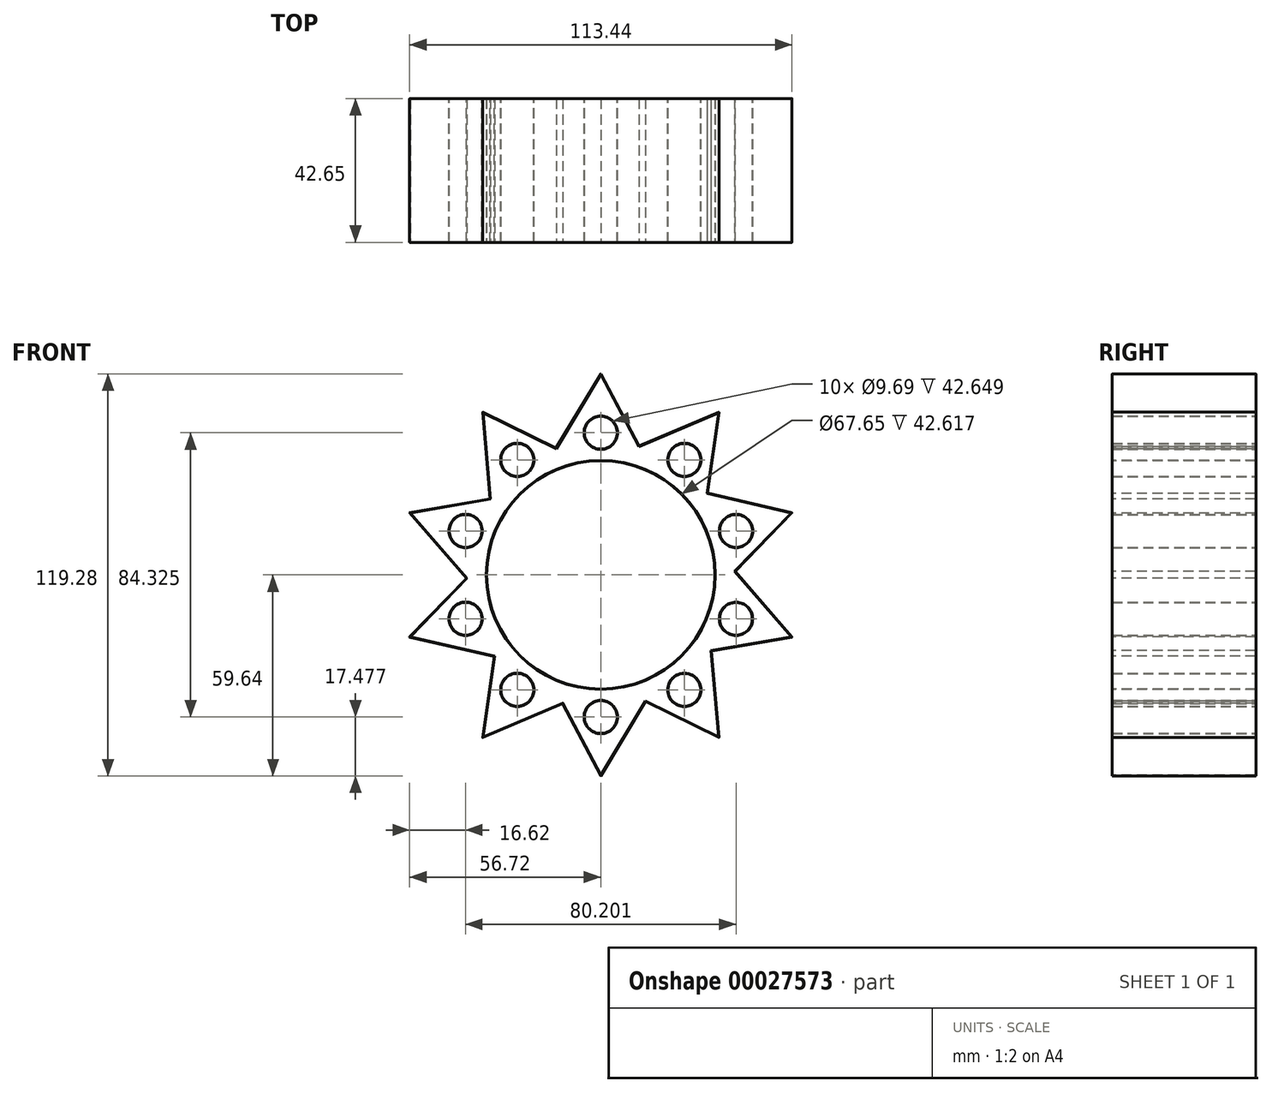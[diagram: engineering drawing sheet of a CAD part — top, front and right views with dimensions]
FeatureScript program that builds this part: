
annotation { "Feature Type Name" : "Feature", "Feature Type Description" : "" }
export const myFeature = defineFeature(function(context is Context, id is Id, definition is map)
    precondition{}
    {
        {
            var Q0;
            Q0=qCreatedBy(makeId("Front.planeOp"),FACE);
            var sketch = newSketch(context, id + "F0", { "sketchPlane" : qUnion([Q0])});
            skCircle(sketch, "E0", {"center": v(0, 0) * mm, "radius": 33.83 * mm});
            skLineSegment(sketch, "E1", {"start": v(-15.28, 34.27) * mm, "end": v(13.84, 33.45) * mm});
            skLineSegment(sketch, "E2", {"start": v(13.84, 33.45) * mm, "end": v(0, 59.67) * mm});
            skLineSegment(sketch, "E3", {"start": v(0, 59.67) * mm, "end": v(-15.28, 34.27) * mm});
            skLineSegment(sketch, "E4.1.0", {"start": v(-8.46, 35.2) * mm, "end": v(-35.07, 48.28) * mm});
            skLineSegment(sketch, "E4.1.1", {"start": v(-35.07, 48.28) * mm, "end": v(-32.5, 18.74) * mm});
            skLineSegment(sketch, "E4.2.0", {"start": v(-27.53, 23.5) * mm, "end": v(-56.75, 18.44) * mm});
            skLineSegment(sketch, "E4.2.1", {"start": v(-56.75, 18.44) * mm, "end": v(-37.31, -3.94) * mm});
            skLineSegment(sketch, "E4.3.0", {"start": v(-36.09, 2.83) * mm, "end": v(-56.75, -18.44) * mm});
            skLineSegment(sketch, "E4.3.1", {"start": v(-56.75, -18.44) * mm, "end": v(-27.87, -25.12) * mm});
            skLineSegment(sketch, "E4.4.0", {"start": v(-30.86, -18.92) * mm, "end": v(-35.07, -48.28) * mm});
            skLineSegment(sketch, "E4.4.1", {"start": v(-35.07, -48.28) * mm, "end": v(-7.78, -36.7) * mm});
            skLineSegment(sketch, "E4.5.0", {"start": v(-13.84, -33.45) * mm, "end": v(0, -59.67) * mm});
            skLineSegment(sketch, "E4.5.1", {"start": v(0, -59.67) * mm, "end": v(15.28, -34.27) * mm});
            skLineSegment(sketch, "E4.6.0", {"start": v(8.46, -35.2) * mm, "end": v(35.07, -48.28) * mm});
            skLineSegment(sketch, "E4.6.1", {"start": v(35.07, -48.28) * mm, "end": v(32.5, -18.74) * mm});
            skLineSegment(sketch, "E4.7.0", {"start": v(27.53, -23.5) * mm, "end": v(56.75, -18.44) * mm});
            skLineSegment(sketch, "E4.7.1", {"start": v(56.75, -18.44) * mm, "end": v(37.31, 3.94) * mm});
            skLineSegment(sketch, "E4.8.0", {"start": v(36.09, -2.83) * mm, "end": v(56.75, 18.44) * mm});
            skLineSegment(sketch, "E4.8.1", {"start": v(56.75, 18.44) * mm, "end": v(27.87, 25.12) * mm});
            skLineSegment(sketch, "E4.9.0", {"start": v(30.86, 18.92) * mm, "end": v(35.07, 48.28) * mm});
            skLineSegment(sketch, "E4.9.1", {"start": v(35.07, 48.28) * mm, "end": v(7.78, 36.7) * mm});
            skSolve(sketch);
        }
        {
            var Q0;
            Q0 = qSketchRegion(id + "F0", true);
            extrude(context, id + "F1", {"entities" : qUnion([Q0]), "oppositeDirection" : true, "depth" : 42.65 * mm});
        }
        {
            var Q0;
            Q0=makeQuery(id+"F1.opExtrude","CAP_FACE",FACE,{"disambiguationData":[OSD([sQuery(id+"F0.wireOp",EDGE,"E0"),sQuery(id+"F0.wireOp",EDGE,"E2"),sQuery(id+"F0.wireOp",EDGE,"E3"),sQuery(id+"F0.wireOp",EDGE,"E4.1.0"),sQuery(id+"F0.wireOp",EDGE,"E4.1.1"),sQuery(id+"F0.wireOp",EDGE,"E4.2.0"),sQuery(id+"F0.wireOp",EDGE,"E4.2.1"),sQuery(id+"F0.wireOp",EDGE,"E4.3.0"),sQuery(id+"F0.wireOp",EDGE,"E4.3.1"),sQuery(id+"F0.wireOp",EDGE,"E4.4.0"),sQuery(id+"F0.wireOp",EDGE,"E4.4.1"),sQuery(id+"F0.wireOp",EDGE,"E4.5.0"),sQuery(id+"F0.wireOp",EDGE,"E4.5.1"),sQuery(id+"F0.wireOp",EDGE,"E4.6.0"),sQuery(id+"F0.wireOp",EDGE,"E4.6.1"),sQuery(id+"F0.wireOp",EDGE,"E4.7.0"),sQuery(id+"F0.wireOp",EDGE,"E4.7.1"),sQuery(id+"F0.wireOp",EDGE,"E4.8.0"),sQuery(id+"F0.wireOp",EDGE,"E4.8.1"),sQuery(id+"F0.wireOp",EDGE,"E4.9.0"),sQuery(id+"F0.wireOp",EDGE,"E4.9.1")])],"isStart":false});
            var sketch = newSketch(context, id + "F2", { "sketchPlane" : qUnion([Q0])});
            skCircle(sketch, "E5", {"center": v(-24.78, -34.11) * mm, "radius": 4.85 * mm});
            skCircle(sketch, "E6.1.0", {"center": v(0, -42.16) * mm, "radius": 4.85 * mm});
            skCircle(sketch, "E6.2.0", {"center": v(24.79, -34.1) * mm, "radius": 4.85 * mm});
            skCircle(sketch, "E6.3.0", {"center": v(40.1, -13.02) * mm, "radius": 4.85 * mm});
            skCircle(sketch, "E6.4.0", {"center": v(40.1, 13.03) * mm, "radius": 4.85 * mm});
            skCircle(sketch, "E6.5.0", {"center": v(24.78, 34.11) * mm, "radius": 4.85 * mm});
            skCircle(sketch, "E6.6.0", {"center": v(0, 42.16) * mm, "radius": 4.85 * mm});
            skCircle(sketch, "E6.7.0", {"center": v(-24.79, 34.1) * mm, "radius": 4.85 * mm});
            skCircle(sketch, "E6.8.0", {"center": v(-40.1, 13.02) * mm, "radius": 4.85 * mm});
            skCircle(sketch, "E6.9.0", {"center": v(-40.1, -13.03) * mm, "radius": 4.85 * mm});
            skPoint(sketch, "E6.center", {"position": v(0, 0) * mm});
            skSolve(sketch);
        }
        {
            var Q0;
            Q0 = qSketchRegion(id + "F2", true);
            extrude(context, id + "F3", {"entities" : qUnion([Q0]), "operationType" : NewBodyOperationType.REMOVE, "endBound" : BoundingType.THROUGH_ALL, "oppositeDirection" : true, "depth" : 25.4 * mm});
        }
        {
            var Q0;
            Q0=makeQuery(id+"F1.opExtrude","CAP_FACE",FACE,{"disambiguationData":[OSD([sQuery(id+"F0.wireOp",EDGE,"E0"),sQuery(id+"F0.wireOp",EDGE,"E2"),sQuery(id+"F0.wireOp",EDGE,"E3"),sQuery(id+"F0.wireOp",EDGE,"E4.1.0"),sQuery(id+"F0.wireOp",EDGE,"E4.1.1"),sQuery(id+"F0.wireOp",EDGE,"E4.2.0"),sQuery(id+"F0.wireOp",EDGE,"E4.2.1"),sQuery(id+"F0.wireOp",EDGE,"E4.3.0"),sQuery(id+"F0.wireOp",EDGE,"E4.3.1"),sQuery(id+"F0.wireOp",EDGE,"E4.4.0"),sQuery(id+"F0.wireOp",EDGE,"E4.4.1"),sQuery(id+"F0.wireOp",EDGE,"E4.5.0"),sQuery(id+"F0.wireOp",EDGE,"E4.5.1"),sQuery(id+"F0.wireOp",EDGE,"E4.6.0"),sQuery(id+"F0.wireOp",EDGE,"E4.6.1"),sQuery(id+"F0.wireOp",EDGE,"E4.7.0"),sQuery(id+"F0.wireOp",EDGE,"E4.7.1"),sQuery(id+"F0.wireOp",EDGE,"E4.8.0"),sQuery(id+"F0.wireOp",EDGE,"E4.8.1"),sQuery(id+"F0.wireOp",EDGE,"E4.9.0"),sQuery(id+"F0.wireOp",EDGE,"E4.9.1")])],"isStart":true});
            shell(context, id + "F4", {"entities" : qUnion([Q0]), "thickness" : 0.13 * mm});
        }
        {
            var Q0;
            Q0=makeQuery(id+"F1.opExtrude","SWEPT_EDGE",EDGE,{"disambiguationData":[OSD([sQuery(id+"F0.wireOp",EDGE,"E4.9.0"),sQuery(id+"F0.wireOp",EDGE,"E4.9.1")])]});
            var Q1;
            Q1=makeQuery(id+"F1.opExtrude","SWEPT_EDGE",EDGE,{"disambiguationData":[OSD([sQuery(id+"F0.wireOp",EDGE,"E4.8.1"),sQuery(id+"F0.wireOp",EDGE,"E4.9.0")])]});
            var Q2;
            Q2=makeQuery(id+"F1.opExtrude","SWEPT_EDGE",EDGE,{"disambiguationData":[OSD([sQuery(id+"F0.wireOp",EDGE,"E4.8.0"),sQuery(id+"F0.wireOp",EDGE,"E4.8.1")])]});
            var Q3;
            Q3=makeQuery(id+"F1.opExtrude","SWEPT_EDGE",EDGE,{"disambiguationData":[OSD([sQuery(id+"F0.wireOp",EDGE,"E4.7.0"),sQuery(id+"F0.wireOp",EDGE,"E4.7.1")])]});
            var Q4;
            Q4=makeQuery(id+"F1.opExtrude","SWEPT_EDGE",EDGE,{"disambiguationData":[OSD([sQuery(id+"F0.wireOp",EDGE,"E4.6.0"),sQuery(id+"F0.wireOp",EDGE,"E4.6.1")])]});
            var Q5;
            Q5=makeQuery(id+"F1.opExtrude","SWEPT_EDGE",EDGE,{"disambiguationData":[OSD([sQuery(id+"F0.wireOp",EDGE,"E4.5.0"),sQuery(id+"F0.wireOp",EDGE,"E4.5.1")])]});
            var Q6;
            Q6=makeQuery(id+"F1.opExtrude","SWEPT_EDGE",EDGE,{"disambiguationData":[OSD([sQuery(id+"F0.wireOp",EDGE,"E4.2.0"),sQuery(id+"F0.wireOp",EDGE,"E4.2.1")])]});
            var Q7;
            Q7=makeQuery(id+"F1.opExtrude","SWEPT_EDGE",EDGE,{"disambiguationData":[OSD([sQuery(id+"F0.wireOp",EDGE,"E4.1.0"),sQuery(id+"F0.wireOp",EDGE,"E4.1.1")])]});
            var Q8;
            Q8=makeQuery(id+"F1.opExtrude","SWEPT_EDGE",EDGE,{"disambiguationData":[OSD([sQuery(id+"F0.wireOp",EDGE,"E2"),sQuery(id+"F0.wireOp",EDGE,"E3")])]});
            var Q9;
            Q9=makeQuery(id+"F1.opExtrude","SWEPT_EDGE",EDGE,{"disambiguationData":[OSD([sQuery(id+"F0.wireOp",EDGE,"E2"),sQuery(id+"F0.wireOp",EDGE,"E4.9.1")])]});
            var Q10;
            Q10=makeQuery(id+"F1.opExtrude","SWEPT_EDGE",EDGE,{"disambiguationData":[OSD([sQuery(id+"F0.wireOp",EDGE,"E4.4.0"),sQuery(id+"F0.wireOp",EDGE,"E4.4.1")])]});
            var Q11;
            Q11=makeQuery(id+"F1.opExtrude","SWEPT_EDGE",EDGE,{"disambiguationData":[OSD([sQuery(id+"F0.wireOp",EDGE,"E4.3.0"),sQuery(id+"F0.wireOp",EDGE,"E4.3.1")])]});
            var Q12;
            Q12=makeQuery(id+"F1.opExtrude","SWEPT_EDGE",EDGE,{"disambiguationData":[OSD([sQuery(id+"F0.wireOp",EDGE,"E4.3.1"),sQuery(id+"F0.wireOp",EDGE,"E4.4.0")])]});
            var Q13;
            Q13=makeQuery(id+"F1.opExtrude","SWEPT_EDGE",EDGE,{"disambiguationData":[OSD([sQuery(id+"F0.wireOp",EDGE,"E4.4.1"),sQuery(id+"F0.wireOp",EDGE,"E4.5.0")])]});
            var Q14;
            Q14=makeQuery(id+"F1.opExtrude","SWEPT_EDGE",EDGE,{"disambiguationData":[OSD([sQuery(id+"F0.wireOp",EDGE,"E4.2.1"),sQuery(id+"F0.wireOp",EDGE,"E4.3.0")])]});
            var Q15;
            Q15=makeQuery(id+"F1.opExtrude","SWEPT_EDGE",EDGE,{"disambiguationData":[OSD([sQuery(id+"F0.wireOp",EDGE,"E4.1.1"),sQuery(id+"F0.wireOp",EDGE,"E4.2.0")])]});
            var Q16;
            Q16=makeQuery(id+"F1.opExtrude","SWEPT_EDGE",EDGE,{"disambiguationData":[OSD([sQuery(id+"F0.wireOp",EDGE,"E3"),sQuery(id+"F0.wireOp",EDGE,"E4.1.0")])]});
            var Q17;
            Q17=makeQuery(id+"F1.opExtrude","SWEPT_EDGE",EDGE,{"disambiguationData":[OSD([sQuery(id+"F0.wireOp",EDGE,"E4.7.1"),sQuery(id+"F0.wireOp",EDGE,"E4.8.0")])]});
            var Q18;
            Q18=makeQuery(id+"F1.opExtrude","SWEPT_EDGE",EDGE,{"disambiguationData":[OSD([sQuery(id+"F0.wireOp",EDGE,"E4.6.1"),sQuery(id+"F0.wireOp",EDGE,"E4.7.0")])]});
            var Q19;
            Q19=makeQuery(id+"F1.opExtrude","SWEPT_EDGE",EDGE,{"disambiguationData":[OSD([sQuery(id+"F0.wireOp",EDGE,"E4.5.1"),sQuery(id+"F0.wireOp",EDGE,"E4.6.0")])]});
            var Q20;
            Q20=makeQuery(id+"F1.opExtrude","CAP_EDGE",EDGE,{"disambiguationData":[OSD([sQuery(id+"F0.wireOp",EDGE,"E4.4.1")])],"isStart":true});
            var Q21;
            {var subQ0=sQuery(id+"F0.wireOp",EDGE,"E4.5.0");Q21=makeQuery(id+"F4.opShell","OFFSET_EDGE",EDGE,{"disambiguationData":[OSD([subQ0]),TDD([makeQuery(id+"F1.opExtrude","CAP_EDGE",EDGE,{"disambiguationData":[OSD([subQ0])],"isStart":true})])]});}
            var Q22;
            Q22=makeQuery(id+"F1.opExtrude","CAP_EDGE",EDGE,{"disambiguationData":[OSD([sQuery(id+"F0.wireOp",EDGE,"E4.5.1")])],"isStart":true});
            var Q23;
            Q23=makeQuery(id+"F1.opExtrude","CAP_EDGE",EDGE,{"disambiguationData":[OSD([sQuery(id+"F0.wireOp",EDGE,"E4.6.0")])],"isStart":true});
            var Q24;
            Q24=makeQuery(id+"F1.opExtrude","CAP_EDGE",EDGE,{"disambiguationData":[OSD([sQuery(id+"F0.wireOp",EDGE,"E4.6.1")])],"isStart":true});
            var Q25;
            Q25=makeQuery(id+"F1.opExtrude","CAP_EDGE",EDGE,{"disambiguationData":[OSD([sQuery(id+"F0.wireOp",EDGE,"E4.7.0")])],"isStart":true});
            var Q26;
            Q26=makeQuery(id+"F1.opExtrude","CAP_EDGE",EDGE,{"disambiguationData":[OSD([sQuery(id+"F0.wireOp",EDGE,"E4.7.1")])],"isStart":true});
            var Q27;
            Q27=makeQuery(id+"F1.opExtrude","CAP_EDGE",EDGE,{"disambiguationData":[OSD([sQuery(id+"F0.wireOp",EDGE,"E4.8.0")])],"isStart":true});
            var Q28;
            Q28=makeQuery(id+"F1.opExtrude","CAP_EDGE",EDGE,{"disambiguationData":[OSD([sQuery(id+"F0.wireOp",EDGE,"E4.8.1")])],"isStart":true});
            var Q29;
            Q29=makeQuery(id+"F1.opExtrude","CAP_EDGE",EDGE,{"disambiguationData":[OSD([sQuery(id+"F0.wireOp",EDGE,"E4.9.0")])],"isStart":true});
            var Q30;
            Q30=makeQuery(id+"F1.opExtrude","CAP_EDGE",EDGE,{"disambiguationData":[OSD([sQuery(id+"F0.wireOp",EDGE,"E4.9.1")])],"isStart":true});
            var Q31;
            Q31=makeQuery(id+"F1.opExtrude","CAP_EDGE",EDGE,{"disambiguationData":[OSD([sQuery(id+"F0.wireOp",EDGE,"E2")])],"isStart":true});
            var Q32;
            Q32=makeQuery(id+"F1.opExtrude","CAP_EDGE",EDGE,{"disambiguationData":[OSD([sQuery(id+"F0.wireOp",EDGE,"E3")])],"isStart":true});
            var Q33;
            Q33=makeQuery(id+"F1.opExtrude","CAP_EDGE",EDGE,{"disambiguationData":[OSD([sQuery(id+"F0.wireOp",EDGE,"E4.1.0")])],"isStart":true});
            var Q34;
            Q34=makeQuery(id+"F1.opExtrude","CAP_EDGE",EDGE,{"disambiguationData":[OSD([sQuery(id+"F0.wireOp",EDGE,"E4.1.1")])],"isStart":true});
            var Q35;
            Q35=makeQuery(id+"F1.opExtrude","CAP_EDGE",EDGE,{"disambiguationData":[OSD([sQuery(id+"F0.wireOp",EDGE,"E4.2.0")])],"isStart":true});
            var Q36;
            Q36=makeQuery(id+"F1.opExtrude","CAP_EDGE",EDGE,{"disambiguationData":[OSD([sQuery(id+"F0.wireOp",EDGE,"E4.2.1")])],"isStart":true});
            var Q37;
            Q37=makeQuery(id+"F1.opExtrude","CAP_EDGE",EDGE,{"disambiguationData":[OSD([sQuery(id+"F0.wireOp",EDGE,"E4.3.0")])],"isStart":true});
            var Q38;
            Q38=makeQuery(id+"F1.opExtrude","CAP_EDGE",EDGE,{"disambiguationData":[OSD([sQuery(id+"F0.wireOp",EDGE,"E4.3.1")])],"isStart":true});
            var Q39;
            Q39=makeQuery(id+"F1.opExtrude","CAP_EDGE",EDGE,{"disambiguationData":[OSD([sQuery(id+"F0.wireOp",EDGE,"E4.4.0")])],"isStart":true});
            var Q40;
            Q40=makeQuery(id+"F1.opExtrude","CAP_EDGE",EDGE,{"disambiguationData":[OSD([sQuery(id+"F0.wireOp",EDGE,"E4.3.1")])],"isStart":false});
            var Q41;
            Q41=makeQuery(id+"F1.opExtrude","CAP_EDGE",EDGE,{"disambiguationData":[OSD([sQuery(id+"F0.wireOp",EDGE,"E4.4.1")])],"isStart":false});
            var Q42;
            Q42=makeQuery(id+"F1.opExtrude","CAP_EDGE",EDGE,{"disambiguationData":[OSD([sQuery(id+"F0.wireOp",EDGE,"E4.5.0")])],"isStart":false});
            var Q43;
            Q43=makeQuery(id+"F1.opExtrude","CAP_EDGE",EDGE,{"disambiguationData":[OSD([sQuery(id+"F0.wireOp",EDGE,"E4.5.1")])],"isStart":false});
            var Q44;
            Q44=makeQuery(id+"F1.opExtrude","CAP_EDGE",EDGE,{"disambiguationData":[OSD([sQuery(id+"F0.wireOp",EDGE,"E4.6.0")])],"isStart":false});
            var Q45;
            Q45=makeQuery(id+"F1.opExtrude","CAP_EDGE",EDGE,{"disambiguationData":[OSD([sQuery(id+"F0.wireOp",EDGE,"E4.7.0")])],"isStart":false});
            var Q46;
            Q46=makeQuery(id+"F1.opExtrude","CAP_EDGE",EDGE,{"disambiguationData":[OSD([sQuery(id+"F0.wireOp",EDGE,"E4.8.0")])],"isStart":false});
            var Q47;
            Q47=makeQuery(id+"F1.opExtrude","CAP_EDGE",EDGE,{"disambiguationData":[OSD([sQuery(id+"F0.wireOp",EDGE,"E4.6.1")])],"isStart":false});
            var Q48;
            Q48=makeQuery(id+"F1.opExtrude","CAP_EDGE",EDGE,{"disambiguationData":[OSD([sQuery(id+"F0.wireOp",EDGE,"E4.7.1")])],"isStart":false});
            var Q49;
            Q49=makeQuery(id+"F1.opExtrude","CAP_EDGE",EDGE,{"disambiguationData":[OSD([sQuery(id+"F0.wireOp",EDGE,"E4.8.1")])],"isStart":false});
            var Q50;
            Q50=makeQuery(id+"F1.opExtrude","CAP_EDGE",EDGE,{"disambiguationData":[OSD([sQuery(id+"F0.wireOp",EDGE,"E4.9.0")])],"isStart":false});
            var Q51;
            Q51=makeQuery(id+"F1.opExtrude","CAP_EDGE",EDGE,{"disambiguationData":[OSD([sQuery(id+"F0.wireOp",EDGE,"E4.9.1")])],"isStart":false});
            var Q52;
            Q52=makeQuery(id+"F1.opExtrude","CAP_EDGE",EDGE,{"disambiguationData":[OSD([sQuery(id+"F0.wireOp",EDGE,"E2")])],"isStart":false});
            var Q53;
            Q53=makeQuery(id+"F1.opExtrude","CAP_EDGE",EDGE,{"disambiguationData":[OSD([sQuery(id+"F0.wireOp",EDGE,"E4.1.0")])],"isStart":false});
            var Q54;
            Q54=makeQuery(id+"F1.opExtrude","CAP_EDGE",EDGE,{"disambiguationData":[OSD([sQuery(id+"F0.wireOp",EDGE,"E4.2.0")])],"isStart":false});
            var Q55;
            Q55=makeQuery(id+"F1.opExtrude","CAP_EDGE",EDGE,{"disambiguationData":[OSD([sQuery(id+"F0.wireOp",EDGE,"E3")])],"isStart":false});
            var Q56;
            Q56=makeQuery(id+"F1.opExtrude","CAP_EDGE",EDGE,{"disambiguationData":[OSD([sQuery(id+"F0.wireOp",EDGE,"E4.2.1")])],"isStart":false});
            var Q57;
            Q57=makeQuery(id+"F1.opExtrude","CAP_EDGE",EDGE,{"disambiguationData":[OSD([sQuery(id+"F0.wireOp",EDGE,"E4.3.0")])],"isStart":false});
            var Q58;
            Q58=makeQuery(id+"F1.opExtrude","CAP_EDGE",EDGE,{"disambiguationData":[OSD([sQuery(id+"F0.wireOp",EDGE,"E4.4.0")])],"isStart":false});
            var Q59;
            Q59=makeQuery(id+"F1.opExtrude","CAP_EDGE",EDGE,{"disambiguationData":[OSD([sQuery(id+"F0.wireOp",EDGE,"E0")])],"isStart":false});
            var Q60;
            Q60=makeQuery(id+"F3.boolean.opBoolean","COPY",EDGE,{"derivedFrom":makeQuery(id+"F3.opExtrude","CAP_EDGE",EDGE,{"disambiguationData":[OSD([sQuery(id+"F2.wireOp",EDGE,"E6.5.0")])],"isStart":true})});
            var Q61;
            Q61=makeQuery(id+"F3.boolean.opBoolean","COPY",EDGE,{"derivedFrom":makeQuery(id+"F3.opExtrude","CAP_EDGE",EDGE,{"disambiguationData":[OSD([sQuery(id+"F2.wireOp",EDGE,"E6.4.0")])],"isStart":true})});
            var Q62;
            Q62=makeQuery(id+"F3.boolean.opBoolean","COPY",EDGE,{"derivedFrom":makeQuery(id+"F3.opExtrude","CAP_EDGE",EDGE,{"disambiguationData":[OSD([sQuery(id+"F2.wireOp",EDGE,"E6.3.0")])],"isStart":true})});
            var Q63;
            Q63=makeQuery(id+"F3.boolean.opBoolean","COPY",EDGE,{"derivedFrom":makeQuery(id+"F3.opExtrude","CAP_EDGE",EDGE,{"disambiguationData":[OSD([sQuery(id+"F2.wireOp",EDGE,"E6.2.0")])],"isStart":true})});
            var Q64;
            Q64=makeQuery(id+"F3.boolean.opBoolean","COPY",EDGE,{"derivedFrom":makeQuery(id+"F3.opExtrude","CAP_EDGE",EDGE,{"disambiguationData":[OSD([sQuery(id+"F2.wireOp",EDGE,"E6.1.0")])],"isStart":true})});
            var Q65;
            Q65=makeQuery(id+"F3.boolean.opBoolean","COPY",EDGE,{"derivedFrom":makeQuery(id+"F3.opExtrude","CAP_EDGE",EDGE,{"disambiguationData":[OSD([sQuery(id+"F2.wireOp",EDGE,"E5")])],"isStart":true})});
            var Q66;
            Q66=makeQuery(id+"F3.boolean.opBoolean","COPY",EDGE,{"derivedFrom":makeQuery(id+"F3.opExtrude","CAP_EDGE",EDGE,{"disambiguationData":[OSD([sQuery(id+"F2.wireOp",EDGE,"E6.9.0")])],"isStart":true})});
            var Q67;
            Q67=makeQuery(id+"F3.boolean.opBoolean","COPY",EDGE,{"derivedFrom":makeQuery(id+"F3.opExtrude","CAP_EDGE",EDGE,{"disambiguationData":[OSD([sQuery(id+"F2.wireOp",EDGE,"E6.8.0")])],"isStart":true})});
            var Q68;
            Q68=makeQuery(id+"F3.boolean.opBoolean","COPY",EDGE,{"derivedFrom":makeQuery(id+"F3.opExtrude","CAP_EDGE",EDGE,{"disambiguationData":[OSD([sQuery(id+"F2.wireOp",EDGE,"E6.7.0")])],"isStart":true})});
            var Q69;
            Q69=makeQuery(id+"F3.boolean.opBoolean","COPY",EDGE,{"derivedFrom":makeQuery(id+"F3.opExtrude","CAP_EDGE",EDGE,{"disambiguationData":[OSD([sQuery(id+"F2.wireOp",EDGE,"E6.6.0")])],"isStart":true})});
            fillet(context, id + "F5", {"entities" : qUnion([Q0, Q1, Q2, Q3, Q4, Q5, Q6, Q7, Q8, Q9, Q10, Q11, Q12, Q13, Q14, Q15, Q16, Q17, Q18, Q19, Q20, Q21, Q22, Q23, Q24, Q25, Q26, Q27, Q28, Q29, Q30, Q31, Q32, Q33, Q34, Q35, Q36, Q37, Q38, Q39, Q40, Q41, Q42, Q43, Q44, Q45, Q46, Q47, Q48, Q49, Q50, Q51, Q52, Q53, Q54, Q55, Q56, Q57, Q58, Q59, Q60, Q61, Q62, Q63, Q64, Q65, Q66, Q67, Q68, Q69]), "radius" : 0.03 * mm, "tangentPropagation" : true, "allowEdgeOverflow" : false});
        }
    });
